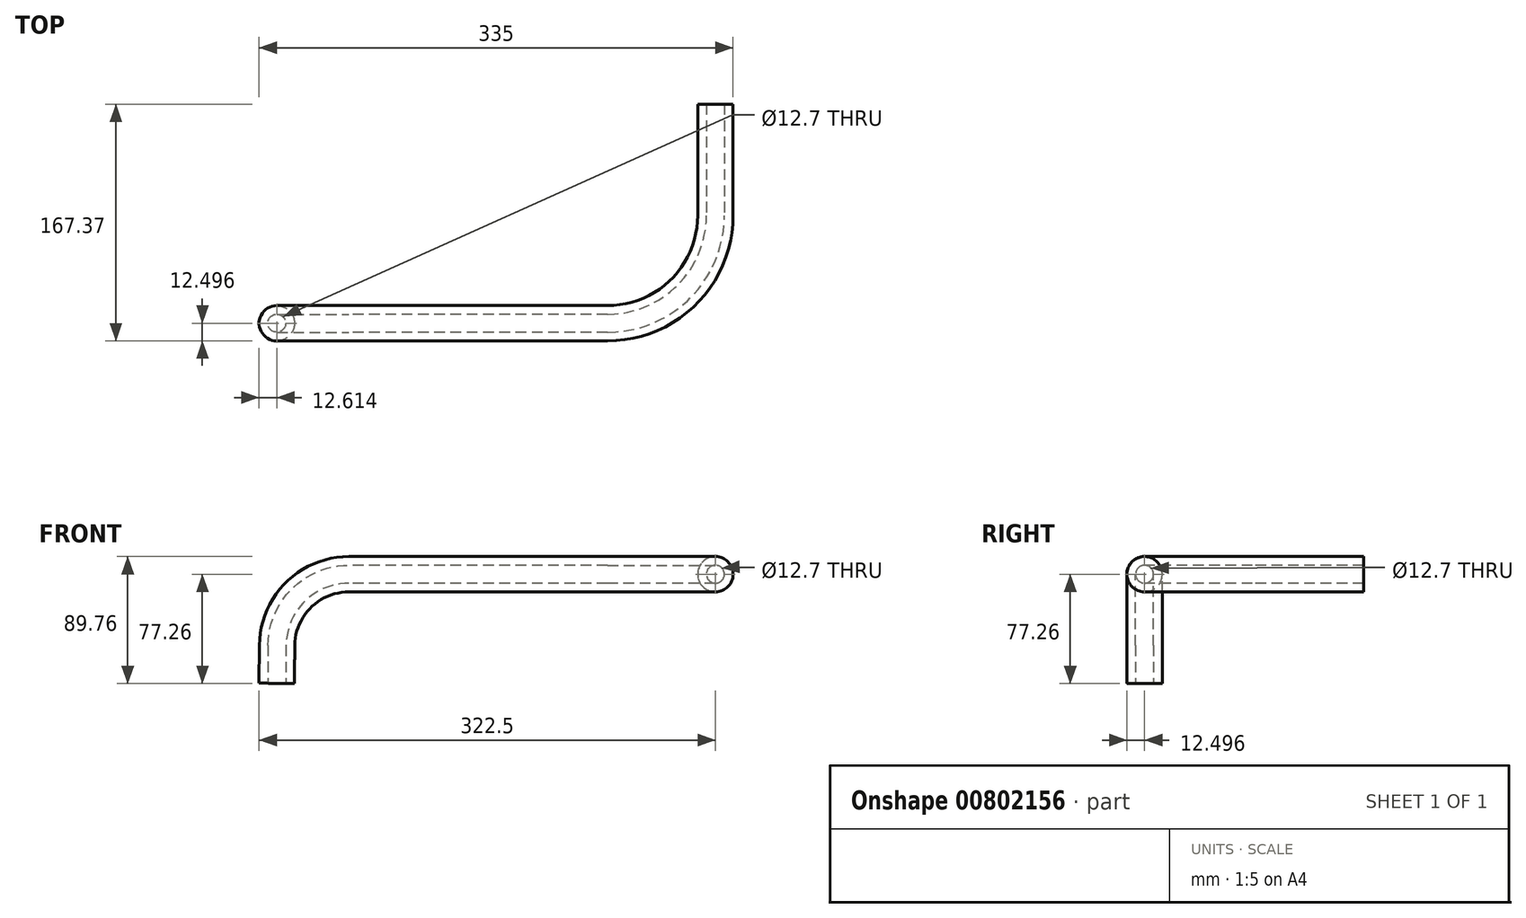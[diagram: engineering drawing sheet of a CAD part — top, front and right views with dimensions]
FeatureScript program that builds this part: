
annotation { "Feature Type Name" : "Feature", "Feature Type Description" : "" }
export const myFeature = defineFeature(function(context is Context, id is Id, definition is map)
    precondition{}
    {
        {
            var Q0;
            Q0=qCreatedBy(makeId("Front.planeOp"),FACE);
            var sketch = newSketch(context, id + "F0", { "sketchPlane" : qUnion([Q0])});
            skCircle(sketch, "E0", {"center": v(0, 0) * mm, "radius": 6.35 * mm});
            skCircle(sketch, "E1", {"center": v(0, 0) * mm, "radius": 12.5 * mm});
            skSolve(sketch);
        }
        {
            var Q0;
            Q0=qCreatedBy(makeId("Top.planeOp"),FACE);
            var sketch = newSketch(context, id + "F1", { "sketchPlane" : qUnion([Q0])});
            skLineSegment(sketch, "E2", {"start": v(0, 0) * mm, "end": v(0, -78.67) * mm});
            skLineSegment(sketch, "E3", {"start": v(-76.2, -154.87) * mm, "end": v(-235.88, -154.87) * mm});
            skPoint(sketch, "E4.visualSharp", {"position": v(0, -154.87) * mm});
            skArc(sketch, "E4.filletArc", {"start": v(-76.2, -154.87) * mm, "mid": v(-22.32, -132.56) * mm, "end": v(0, -78.67) * mm});
            skSolve(sketch);
        }
        {
            var Q0;
            Q0=qCreatedBy(makeId("Front.planeOp"),FACE);
            cPlane(context, id + "F2", {"entities" : qUnion([Q0]), "cplaneType" : CPlaneType.OFFSET, "offset" : 154.87 * mm, "width" : 150 * mm, "height" : 150 * mm});
        }
        {
            var Q0;
            Q0=qCreatedBy(id+"F2.planeOp",FACE);
            var sketch = newSketch(context, id + "F3", { "sketchPlane" : qUnion([Q0])});
            skLineSegment(sketch, "E5", {"start": v(-235.88, 0) * mm, "end": v(-258.98, 0) * mm});
            skLineSegment(sketch, "E6", {"start": v(-310, -77.15) * mm, "end": v(-309.77, -50.37) * mm});
            skPoint(sketch, "E7.newPointA", {"position": v(-309.24, 13.06) * mm});
            skPoint(sketch, "E7.newPointB", {"position": v(-309.24, 0) * mm});
            skArc(sketch, "E7.filletArc", {"start": v(-258.98, 0) * mm, "mid": v(-294.74, -14.73) * mm, "end": v(-309.77, -50.37) * mm});
            skSolve(sketch);
        }
        {
            var Q0;
            Q0=qSketchRegion(id+"F0",true);
            var Q1;
            Q1=qConstructionFilter(qBodyType(qCreatedBy(id+"F1",EDGE),BodyType.WIRE),ConstructionObject.NO);
            var Q2;
            Q2=qConstructionFilter(qBodyType(qCreatedBy(id+"F3",EDGE),BodyType.WIRE),ConstructionObject.NO);
            sweep(context, id + "F4", {"profiles" : qUnion([Q0]), "path" : qUnion([Q1, Q2])});
        }
    });
